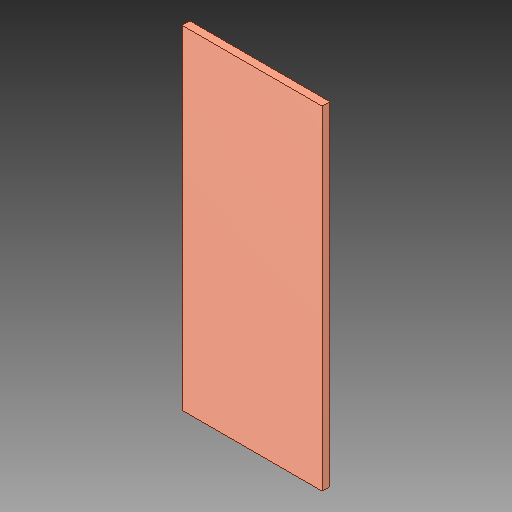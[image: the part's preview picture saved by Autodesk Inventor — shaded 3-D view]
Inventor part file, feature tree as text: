
AUTODESK INVENTOR PART (.ipt)
format: ipt  version: 2019 (Build 230136000, 136)  size: 84,992 bytes
history: native  units: in
note: dims shown in document units (in); Inventor stores cm internally (conversion verified against a paired STEP export)
features: extrude x1, other x1
ambient origin geometry x8: Origin, YZ Plane, XZ Plane, XY Plane, X Axis, Y Axis, Z Axis, Center Point
bodies: Solid1 (feature_tree)
feature tree (2):
  extrude  "Extrusion1"  Depth=0.0394in TaperAngle=0.0deg
  other  "E01-ML01DP5, E01-ML01DP5_23"
